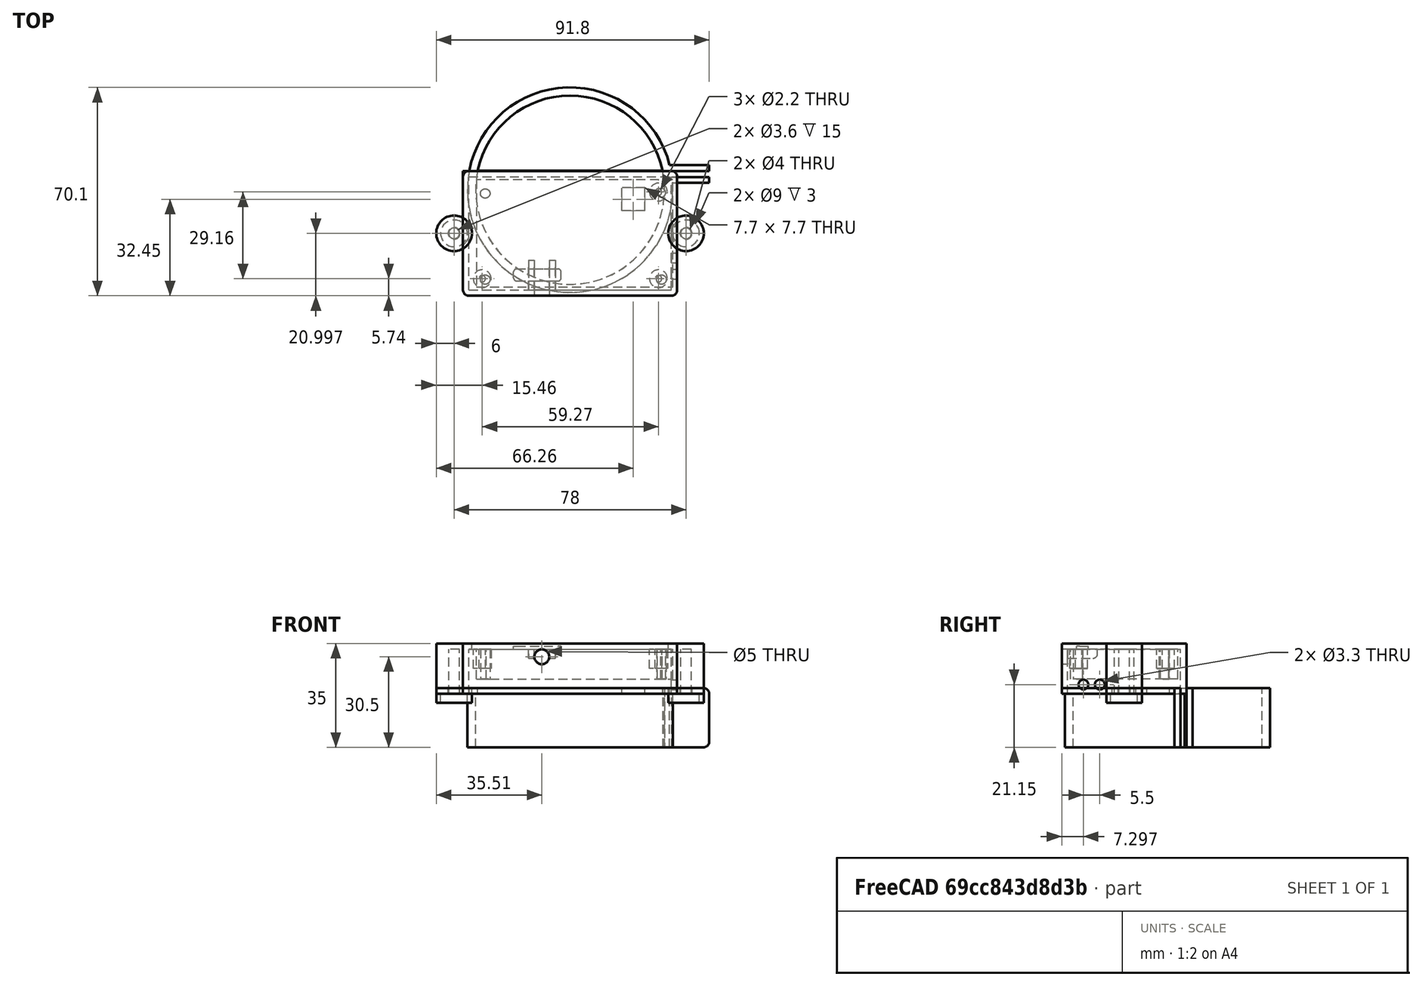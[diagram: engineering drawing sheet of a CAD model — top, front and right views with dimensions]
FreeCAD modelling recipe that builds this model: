
FCSTD DOCUMENT  (FreeCAD 0.18R4 (GitTag))
Label: CASE in FreeCAD
License: All rights reserved
LicenseURL: http://en.wikipedia.org/wiki/All_rights_reserved
objects: Part::Cylinder×22, Part::Cut×19, Part::Box×15, Part::MultiFuse×12, Part::Extrusion×12, Part::Part2DObjectPython×8, Part::Fillet×7, Part::Feature×4, Part::Fuse×2
note: 101 computed .brp shape members not serialized (recipe doc carries the construction recipe); baked Part::Feature solids carry a one-line shape summary decoded from their .brp

FEATURE [Part::Cylinder] Cylinder
  Angle = 360
  AttacherType = Attacher::AttachEngine3D
  Height = 18
  Radius = 31.75
FEATURE [Part::Cylinder] Cylinder001
  Angle = 360
  AttacherType = Attacher::AttachEngine3D
  Height = 20
  Radius = 34.5
FEATURE [Part::Cylinder] Cylinder002
  Angle = 360
  AttacherType = Attacher::AttachEngine3D
  Height = 25
  Radius = 31.75
FEATURE [Part::Box] Box  label="Kostka"
  AttacherType = Attacher::AttachEngine3D
  Height = 25
  Length = 80
  Placement = pos=(-38,-32.5,0) rot=(0,0,1;0rad)
  Width = 39
FEATURE [Part::Box] Box001  label="Kostka001"
  AttacherType = Attacher::AttachEngine3D
  Height = 10
  Length = 7.7
  Placement = pos=(25.1,-7,10) rot=(0,0,1;1.5708rad)
  Width = 7.7
FEATURE [Part::Box] Box002  label="Kostka002"
  AttacherType = Attacher::AttachEngine3D
  Height = 20
  Length = 10
  Placement = pos=(31.2216,4.36291,0) rot=(0,0,1;0rad)
  Width = 2
FEATURE [Part::Box] Box005  label="Kostka005"
  AttacherType = Attacher::AttachEngine3D
  Height = 20
  Length = 15
  Placement = pos=(31.79,6.35995,0) rot=(0,0,1;0rad)
  Width = 2
FEATURE [Part::Box] Box006  label="Kostka006"
  AttacherType = Attacher::AttachEngine3D
  Height = 20
  Length = 15
  Placement = pos=(31.7936,2.35995,0) rot=(0,0,1;0rad)
  Width = 2
FEATURE [Part::Box] Box007  label="Kostka007"
  AttacherType = Attacher::AttachEngine3D
  Height = 2
  Length = 72
  Placement = pos=(-36.01,-35.6034,18) rot=(0,0,1;0rad)
  Width = 42
FEATURE [Part::Cut] Cut
  Base = -> Cylinder001
  Tool = -> Cylinder
FEATURE [Part::Cut] Cut001
  Base = -> Cylinder002
  Tool = -> Box
FEATURE [Part::MultiFuse] Fusion
  Shapes = -> [Cut,Box007]
FEATURE [Part::Cut] Cut002
  Base = -> Fusion
  Tool = -> Box001
FEATURE [Part::Cut] Cut003
  Base = -> Cut002
  Tool = -> Cut001
FEATURE [Part::Cut] Cut004
  Base = -> Cut003
  Tool = -> Box002
FEATURE [Part::Box] Box008  label="Kostka008"
  AttacherType = Attacher::AttachEngine3D
  Height = 17
  Length = 72
  Placement = pos=(-36.01,-35.6034,18) rot=(0,0,1;0rad)
  Width = 42
FEATURE [Part::Box] Box009  label="Kostka009"
  AttacherType = Attacher::AttachEngine3D
  Height = 15
  Length = 68
  Placement = pos=(-34.01,-33.6034,18) rot=(0,0,1;0rad)
  Width = 38
FEATURE [Part::Fillet] Fillet001
  Base = -> Cut004
  Edges = 2 edges r=2: [Edge1,Edge6]
FEATURE [Part::Fillet] Fillet002
  Base = -> Box005
  Edges = 2 edges r=2: [Edge6,Edge8]
FEATURE [Part::Fillet] Fillet003
  Base = -> Box006
  Edges = 2 edges r=2: [Edge6,Edge8]
FEATURE [Part::Fuse] Fusion001
  Base = -> Fillet001
  Tool = -> Fillet002
FEATURE [Part::Fuse] Fusion002  label="PODST"
  Base = -> Fillet003
  Tool = -> Fusion001
FEATURE [Part::Cut] Cut005
  Base = -> Box008
  Tool = -> Box009
FEATURE [Part::Fillet] Fillet  label="POKRYWA_1"
  Base = -> Cut005
  Edges = 4 edges r=2: [Edge1,Edge3,Edge6,Edge11]
FEATURE [Part::Part2DObjectPython] Circle001  # Draft 2D object (typed FeaturePython)
  FirstAngle = 0
  LastAngle = 0
  MakeFace = false
  Placement = pos=(130.06,-64.7857,0) rot=(0,0,1;0rad)
  Radius = 0.5
FEATURE [Part::Part2DObjectPython] Circle002  # Draft 2D object (typed FeaturePython)
  FirstAngle = 0
  LastAngle = 0
  MakeFace = false
  Placement = pos=(70.7984,-64.7696,0) rot=(0,0,1;0rad)
  Radius = 0.5
FEATURE [Part::Part2DObjectPython] Circle  # Draft 2D object (typed FeaturePython)
  FirstAngle = 0
  LastAngle = 0
  MakeFace = false
  Placement = pos=(130.059,-35.5556,0) rot=(0,0,1;0rad)
  Radius = 0.5
FEATURE [Part::Part2DObjectPython] Rectangle  # Draft 2D object (typed FeaturePython)
  ChamferSize = 0
  Columns = 1
  FilletRadius = 0
  Height = 36
  Length = 66
  MakeFace = false
  Placement = pos=(67.8363,-67.2127,0) rot=(0,0,1;0rad)
  Rows = 1
FEATURE [Part::Part2DObjectPython] Circle003  # Draft 2D object (typed FeaturePython)
  FirstAngle = 0
  LastAngle = 0
  MakeFace = false
  Placement = pos=(70.7901,-35.8008,0) rot=(0,0,1;0rad)
  Radius = 0.5
FEATURE [Part::Extrusion] Extrude093
  Base = -> Circle
  Dir = (0,0,1)
  DirMode = 0
  FaceMakerClass = Part::FaceMakerBullseye
  LengthFwd = 10
  LengthRev = 0
  Solid = true
  Symmetric = false
FEATURE [Part::Extrusion] Extrude095
  Base = -> Circle002
  Dir = (0,0,1)
  DirMode = 0
  FaceMakerClass = Part::FaceMakerBullseye
  LengthFwd = 10
  LengthRev = 0
  Solid = true
  Symmetric = false
FEATURE [Part::Extrusion] Extrude096
  Base = -> Circle003
  Dir = (0,0,1)
  DirMode = 0
  FaceMakerClass = Part::FaceMakerBullseye
  LengthFwd = 10
  LengthRev = 0
  Solid = true
  Symmetric = false
FEATURE [Part::Extrusion] Extrude094
  Base = -> Circle001
  Dir = (0,0,1)
  DirMode = 0
  FaceMakerClass = Part::FaceMakerBullseye
  LengthFwd = 10
  LengthRev = 0
  Solid = true
  Symmetric = false
FEATURE [Part::Extrusion] Extrude097
  Base = -> Rectangle
  Dir = (0,0,1)
  DirMode = 0
  FaceMakerClass = Part::FaceMakerBullseye
  LengthFwd = 10
  LengthRev = 0
  Solid = true
  Symmetric = false
FEATURE [Part::MultiFuse] Fusion003  label="PCB"
  Placement = pos=(-99.3416,34.6093,23) rot=(0,0,1;0rad)
  Shapes = -> [Extrude093,Extrude094,Extrude095,Extrude096,Extrude097]
FEATURE [Part::Feature] path847010
  shape: bbox 3.193 x 3.179 x 2e-07 mm, 1 faces, 0 solids (baked)
FEATURE [Part::Feature] path847007
  shape: bbox 2.86 x 2.857 x 2e-07 mm, 1 faces, 0 solids (baked)
FEATURE [Part::Feature] path847090
  shape: bbox 3.193 x 3.187 x 2e-07 mm, 1 faces, 0 solids (baked)
FEATURE [Part::Feature] path847092
  shape: bbox 3.193 x 3.187 x 2e-07 mm, 1 faces, 0 solids (baked)
FEATURE [Part::Extrusion] Extrude005
  Base = -> path847007
  Dir = (0,0,1)
  DirMode = 0
  FaceMakerClass = Part::FaceMakerBullseye
  LengthFwd = 10
  LengthRev = 0
  Solid = false
  Symmetric = false
FEATURE [Part::Extrusion] Extrude008
  Base = -> path847010
  Dir = (0,0,1)
  DirMode = 0
  FaceMakerClass = Part::FaceMakerBullseye
  LengthFwd = 10
  LengthRev = 0
  Solid = false
  Symmetric = false
FEATURE [Part::Extrusion] Extrude090
  Base = -> path847092
  Dir = (0,0,1)
  DirMode = 0
  FaceMakerClass = Part::FaceMakerBullseye
  LengthFwd = 10
  LengthRev = 0
  Solid = false
  Symmetric = false
FEATURE [Part::Extrusion] Extrude088
  Base = -> path847090
  Dir = (0,0,1)
  DirMode = 0
  FaceMakerClass = Part::FaceMakerBullseye
  LengthFwd = 10
  LengthRev = 0
  Solid = false
  Symmetric = false
FEATURE [Part::MultiFuse] Fusion004  label="PCB_HOLES"
  Placement = pos=(-99.3416,34.6093,23) rot=(0,0,1;0rad)
  Shapes = -> [Extrude008,Extrude088,Extrude005,Extrude090]
FEATURE [Part::Part2DObjectPython] Circle004  # Draft 2D object (typed FeaturePython)
  FirstAngle = 0
  LastAngle = 0
  MakeFace = false
  Placement = pos=(-28.5503,-30.1605,33) rot=(1,0,0;3.14159rad)
  Radius = 3
FEATURE [Part::Part2DObjectPython] Circle006  # Draft 2D object (typed FeaturePython)
  FirstAngle = 0
  LastAngle = 0
  MakeFace = false
  Placement = pos=(30.7196,-1,33) rot=(1,0,0;3.14159rad)
  Radius = 3
FEATURE [Part::Part2DObjectPython] Circle007  # Draft 2D object (typed FeaturePython)
  FirstAngle = 0
  LastAngle = 0
  MakeFace = false
  Placement = pos=(30.7196,-30.1605,33) rot=(1,0,0;3.14159rad)
  Radius = 3
FEATURE [Part::Extrusion] Extrude
  Base = -> Circle004
  Dir = (0,0,-1)
  DirMode = 0
  FaceMakerClass = Part::FaceMakerBullseye
  LengthFwd = 6.5
  LengthRev = 0
  Solid = true
  Symmetric = false
FEATURE [Part::Extrusion] Extrude099
  Base = -> Circle006
  Dir = (0,0,-1)
  DirMode = 0
  FaceMakerClass = Part::FaceMakerBullseye
  LengthFwd = 6.5
  LengthRev = 0
  Solid = true
  Symmetric = false
FEATURE [Part::Extrusion] Extrude100
  Base = -> Circle007
  Dir = (0,0,-1)
  DirMode = 0
  FaceMakerClass = Part::FaceMakerBullseye
  LengthFwd = 6.5
  LengthRev = 0
  Solid = true
  Symmetric = false
FEATURE [Part::MultiFuse] Fusion005
  Shapes = -> [Extrude,Extrude099,Extrude100]
FEATURE [Part::Cylinder] Cylinder003
  Angle = 360
  AttacherType = Attacher::AttachEngine3D
  Height = 6.5
  Placement = pos=(-28.5503,-1,26.5) rot=(0,0,1;0rad)
  Radius = 1.1
FEATURE [Part::Cylinder] Cylinder004
  Angle = 360
  AttacherType = Attacher::AttachEngine3D
  Height = 6.5
  Placement = pos=(-28.5503,-30.1605,26.5) rot=(0,0,1;0rad)
  Radius = 1.1
FEATURE [Part::Cylinder] Cylinder005
  Angle = 360
  AttacherType = Attacher::AttachEngine3D
  Height = 6.5
  Placement = pos=(30.7196,-30.1605,26.5) rot=(0,0,1;0rad)
  Radius = 1.1
FEATURE [Part::Cylinder] Cylinder006
  Angle = 360
  AttacherType = Attacher::AttachEngine3D
  Height = 6.5
  Placement = pos=(30.7196,-1,26.5) rot=(0,0,1;0rad)
  Radius = 1.1
FEATURE [Part::MultiFuse] Fusion006
  Shapes = -> [Cylinder003,Cylinder006,Cylinder005,Cylinder004]
FEATURE [Part::Cut] Cut006  label="PCB MOUNT"
  Base = -> Fusion005
  Placement = pos=(-1,0.3,0) rot=(0,0,1;0rad)
  Tool = -> Fusion006
FEATURE [Part::Cylinder] Cylinder010
  Angle = 360
  AttacherType = Attacher::AttachEngine3D
  Height = 5
  Placement = pos=(-39.01,-14.6034,15) rot=(0,0,1;0rad)
  Radius = 6
FEATURE [Part::Cylinder] Cylinder011
  Angle = 360
  AttacherType = Attacher::AttachEngine3D
  Height = 5
  Placement = pos=(-39.01,-14.6034,15) rot=(0,0,1;0rad)
  Radius = 2
FEATURE [Part::Cylinder] Cylinder012
  Angle = 360
  AttacherType = Attacher::AttachEngine3D
  Height = 3
  Placement = pos=(-39.01,-14.6034,15) rot=(0,0,1;0rad)
  Radius = 4.5
FEATURE [Part::Cut] Cut009
  Base = -> Cylinder010
  Tool = -> Cylinder012
FEATURE [Part::Cut] Cut010
  Base = -> Cut009
  Tool = -> Cylinder011
FEATURE [Part::Cylinder] Cylinder013
  Angle = 360
  AttacherType = Attacher::AttachEngine3D
  Height = 3
  Placement = pos=(-39.01,-14.6034,15) rot=(0,0,1;0rad)
  Radius = 4.5
FEATURE [Part::Cylinder] Cylinder014
  Angle = 360
  AttacherType = Attacher::AttachEngine3D
  Height = 5
  Placement = pos=(-39.01,-14.6034,15) rot=(0,0,1;0rad)
  Radius = 2
FEATURE [Part::Box] Box011  label="Kostka011"
  AttacherType = Attacher::AttachEngine3D
  Height = 17
  Length = 5
  Placement = pos=(-39.01,-17.1034,18) rot=(0,0,1;0rad)
  Width = 5
FEATURE [Part::Cylinder] Cylinder016
  Angle = 360
  AttacherType = Attacher::AttachEngine3D
  Height = 15
  Placement = pos=(-39.01,-14.6034,18) rot=(0,0,1;0rad)
  Radius = 1.8
FEATURE [Part::Cylinder] Cylinder017
  Angle = 360
  AttacherType = Attacher::AttachEngine3D
  Height = 17
  Placement = pos=(-39.01,-14.6034,18) rot=(0,0,1;0rad)
  Radius = 6
FEATURE [Part::Cylinder] Cylinder018
  Angle = 360
  AttacherType = Attacher::AttachEngine3D
  Height = 5
  Placement = pos=(-39.01,-14.6034,15) rot=(0,0,1;0rad)
  Radius = 6
FEATURE [Part::Cut] Cut011
  Base = -> Cylinder018
  Tool = -> Cylinder013
FEATURE [Part::Cut] Cut012
  Base = -> Cut011
  Placement = pos=(-0.02,-29.2068,0) rot=(0,0,1;3.14159rad)
  Tool = -> Cylinder014
FEATURE [Part::Cylinder] Cylinder019
  Angle = 360
  AttacherType = Attacher::AttachEngine3D
  Height = 5
  Placement = pos=(38.99,-14.6034,15) rot=(0,0,1;0rad)
  Radius = 5
FEATURE [Part::Cylinder] Cylinder020
  Angle = 360
  AttacherType = Attacher::AttachEngine3D
  Height = 5
  Placement = pos=(-39.01,-14.6034,15) rot=(0,0,1;0rad)
  Radius = 5
FEATURE [Part::MultiFuse] Fusion013
  Shapes = -> [Cylinder019,Cylinder020]
FEATURE [Part::Cut] Cut015  label="BASE"
  Base = -> Fusion002
  Tool = -> Fusion013
FEATURE [Part::Cylinder] Cylinder021
  Angle = 360
  AttacherType = Attacher::AttachEngine3D
  Height = 17
  Placement = pos=(38.99,-14.6034,18) rot=(0,0,1;0rad)
  Radius = 6
FEATURE [Part::Box] Box012  label="Kostka012"
  AttacherType = Attacher::AttachEngine3D
  Height = 17
  Length = 5
  Placement = pos=(34.0681,-17.1,18) rot=(0,0,1;0rad)
  Width = 5
FEATURE [Part::Cylinder] Cylinder022
  Angle = 360
  AttacherType = Attacher::AttachEngine3D
  Height = 15
  Placement = pos=(38.99,-14.6034,18) rot=(0,0,1;0rad)
  Radius = 1.8
FEATURE [Part::MultiFuse] Fusion012  label="BASE MOUNT"
  Shapes = -> [Cut012,Cut010]
FEATURE [Part::MultiFuse] Fusion014
  Shapes = -> [Box011,Cylinder017]
FEATURE [Part::MultiFuse] Fusion015
  Shapes = -> [Box012,Cylinder021]
FEATURE [Part::Cut] Cut016
  Base = -> Fusion014
  Tool = -> Cylinder016
FEATURE [Part::Cut] Cut017
  Base = -> Fusion015
  Tool = -> Cylinder022
FEATURE [Part::Box] Box013  label="Kostka013"
  AttacherType = Attacher::AttachEngine3D
  Height = 15
  Length = 10
  Placement = pos=(-34.01,-19.6034,18) rot=(0,0,1;0rad)
  Width = 10
FEATURE [Part::Box] Box014  label="Kostka014"
  AttacherType = Attacher::AttachEngine3D
  Height = 15
  Length = 10
  Placement = pos=(23.99,-19.6034,18) rot=(0,0,1;0rad)
  Width = 10
FEATURE [Part::Cut] Cut018
  Base = -> Cut016
  Tool = -> Box013
FEATURE [Part::Cut] Cut019
  Base = -> Cut017
  Tool = -> Box014
FEATURE [Part::MultiFuse] Fusion016  label="COVER MOUNT"
  Shapes = -> [Cut018,Cut019]
FEATURE [Part::Cylinder] Cylinder023
  Angle = 360
  AttacherType = Attacher::AttachEngine3D
  Height = 2
  Placement = pos=(-9.5,-33.6034,30.5) rot=(1,0,0;1.5708rad)
  Radius = 2.5
FEATURE [Part::Box] Box015  label="Kostka015"
  AttacherType = Attacher::AttachEngine3D
  Height = 5
  Length = 2
  Placement = pos=(-14,-33.6,30) rot=(0,0,1;0rad)
  Width = 10
FEATURE [Part::Box] Box017  label="Kostka017"
  AttacherType = Attacher::AttachEngine3D
  Height = 1
  Length = 16
  Placement = pos=(-19,-30.6,33) rot=(0,0,1;0rad)
  Width = 4
FEATURE [Part::Box] Box018  label="Kostka018"
  AttacherType = Attacher::AttachEngine3D
  Height = 5
  Length = 2
  Placement = pos=(-7,-33.6,30) rot=(0,0,1;0rad)
  Width = 10
FEATURE [Part::Cut] Cut020
  Base = -> Fillet
  Tool = -> Cylinder023
FEATURE [Part::Fillet] Fillet004
  Base = -> Box017
  Edges = 4 edges r=1: [Edge1,Edge3,Edge5,Edge7]
FEATURE [Part::Fillet] Fillet005
  Base = -> Box018
  Edges = 1 edges r=1.5: [Edge11]
FEATURE [Part::Fillet] Fillet006
  Base = -> Box015
  Edges = 1 edges r=1.5: [Edge11]
FEATURE [Part::MultiFuse] Fusion017
  Shapes = -> [Fillet005,Fillet006,Cut020]
FEATURE [Part::Cylinder] Cylinder024
  Angle = 360
  AttacherType = Attacher::AttachEngine3D
  Height = 10
  Placement = pos=(33.99,-28.3034,21.15) rot=(0,1,0;1.5708rad)
  Radius = 1.65
FEATURE [Part::Cylinder] Cylinder025
  Angle = 360
  AttacherType = Attacher::AttachEngine3D
  Height = 10
  Placement = pos=(33.99,-22.8034,21.15) rot=(0,1,0;1.5708rad)
  Radius = 1.65
FEATURE [Part::MultiFuse] Fusion018
  Shapes = -> [Cylinder024,Cylinder025]
FEATURE [Part::Cut] Cut021
  Base = -> Fusion017
  Tool = -> Fusion018
FEATURE [Part::Cut] Cut022  label="COVER"
  Base = -> Cut021
  Tool = -> Fillet004
